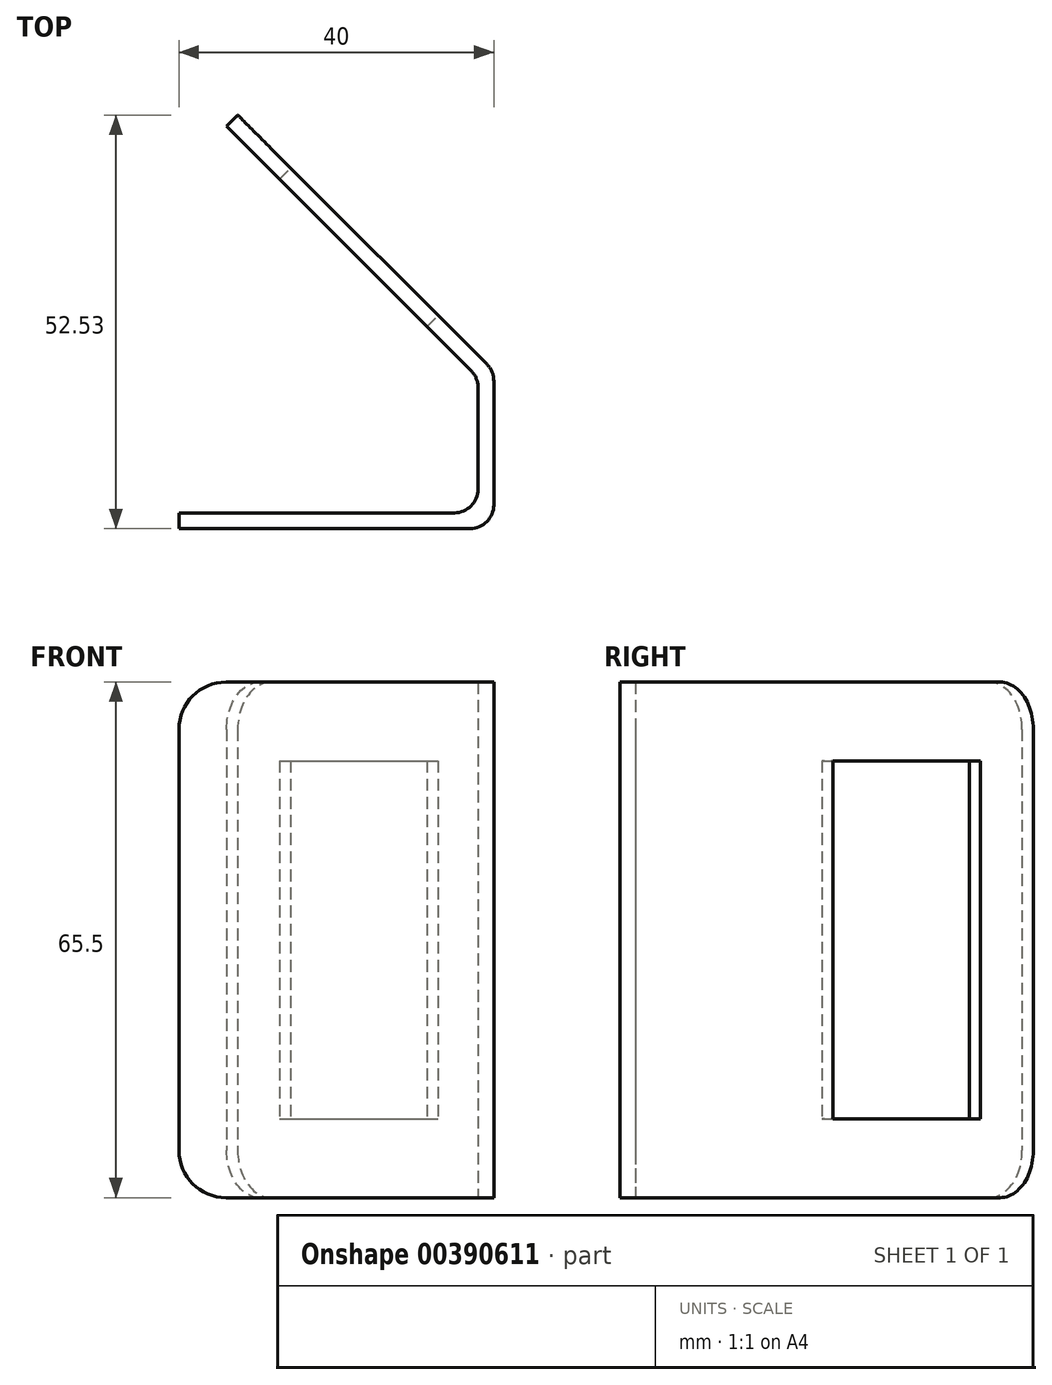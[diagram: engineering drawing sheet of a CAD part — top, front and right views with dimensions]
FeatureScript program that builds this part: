
annotation { "Feature Type Name" : "Feature", "Feature Type Description" : "" }
export const myFeature = defineFeature(function(context is Context, id is Id, definition is map)
    precondition{}
    {
        {
            var Q0;
            Q0=qCreatedBy(makeId("Top.planeOp"),FACE);
            var sketch = newSketch(context, id + "F0", { "sketchPlane" : qUnion([Q0])});
            skLineSegment(sketch, "E0", {"start": v(0, 0) * mm, "end": v(40, 0) * mm});
            skLineSegment(sketch, "E1", {"start": v(40, 0) * mm, "end": v(40, 20) * mm});
            skLineSegment(sketch, "E2", {"start": v(40, 20) * mm, "end": v(7.47, 52.53) * mm});
            skLineSegment(sketch, "E3", {"start": v(49.42, 20) * mm, "end": v(-18.7, 20) * mm, "construction": true});
            skLineSegment(sketch, "E4", {"start": v(7.47, 52.53) * mm, "end": v(6.06, 51.11) * mm});
            skLineSegment(sketch, "E5", {"start": v(6.06, 51.11) * mm, "end": v(38, 19.17) * mm});
            skLineSegment(sketch, "E6", {"start": v(38, 19.17) * mm, "end": v(38, 2) * mm});
            skLineSegment(sketch, "E7", {"start": v(38, 2) * mm, "end": v(0, 2) * mm});
            skLineSegment(sketch, "E8", {"start": v(0, 2) * mm, "end": v(0, 0) * mm});
            skSolve(sketch);
        }
        {
            var Q0;
            Q0=makeQuery(id+"F0.imprint","IMPRINT",FACE,{"disambiguationData":[TD([[makeQuery(id+"F0.imprint","IMPRINT",EDGE,{"derivedFrom":sQuery(id+"F0.wireOp",EDGE,"E0")}),1.0]])]});
            extrude(context, id + "F1", {"entities" : qUnion([Q0]), "depth" : 65.5 * mm, "offsetDistance" : 25 * mm});
        }
        {
            var Q0;
            Q0=makeQuery(id+"F1.opExtrude","SWEPT_FACE",FACE,{"disambiguationData":[OSD([sQuery(id+"F0.wireOp",EDGE,"E2")])]});
            var sketch = newSketch(context, id + "F2", { "sketchPlane" : qUnion([Q0])});
            skLineSegment(sketch, "E9.bottom", {"start": v(22.36, 55.5) * mm, "end": v(-4.14, 55.5) * mm});
            skLineSegment(sketch, "E9.top", {"start": v(22.36, 10) * mm, "end": v(-4.14, 10) * mm});
            skLineSegment(sketch, "E9.left", {"start": v(22.36, 55.5) * mm, "end": v(22.36, 10) * mm});
            skLineSegment(sketch, "E9.right", {"start": v(-4.14, 55.5) * mm, "end": v(-4.14, 10) * mm});
            skSolve(sketch);
        }
        {
            var Q0;
            Q0=makeQuery(id+"F2.imprint","IMPRINT",FACE,{"disambiguationData":[TD([[makeQuery(id+"F2.imprint","IMPRINT",EDGE,{"derivedFrom":sQuery(id+"F2.wireOp",EDGE,"E9.bottom")}),1.0]])]});
            extrude(context, id + "F3", {"entities" : qUnion([Q0]), "operationType" : NewBodyOperationType.REMOVE, "oppositeDirection" : true, "depth" : 5 * mm, "offsetDistance" : 25 * mm});
        }
        {
            var Q0;
            Q0=makeQuery(id+"F1.opExtrude","CAP_EDGE",EDGE,{"disambiguationData":[OSD([sQuery(id+"F0.wireOp",EDGE,"E4")])],"isStart":false});
            var Q1;
            Q1=makeQuery(id+"F1.opExtrude","CAP_EDGE",EDGE,{"disambiguationData":[OSD([sQuery(id+"F0.wireOp",EDGE,"E4")])],"isStart":true});
            var Q2;
            Q2=makeQuery(id+"F1.opExtrude","CAP_EDGE",EDGE,{"disambiguationData":[OSD([sQuery(id+"F0.wireOp",EDGE,"E8")])],"isStart":true});
            var Q3;
            Q3=makeQuery(id+"F1.opExtrude","CAP_EDGE",EDGE,{"disambiguationData":[OSD([sQuery(id+"F0.wireOp",EDGE,"E8")])],"isStart":false});
            fillet(context, id + "F4", {"entities" : qUnion([Q0, Q1, Q2, Q3]), "radius" : 6 * mm, "tangentPropagation" : true, "allowEdgeOverflow" : false});
        }
        {
            var Q0;
            Q0=makeQuery(id+"F1.opExtrude","SWEPT_EDGE",EDGE,{"disambiguationData":[OSD([sQuery(id+"F0.wireOp",EDGE,"E1"),sQuery(id+"F0.wireOp",EDGE,"E2")])]});
            var Q1;
            Q1=makeQuery(id+"F1.opExtrude","SWEPT_EDGE",EDGE,{"disambiguationData":[OSD([sQuery(id+"F0.wireOp",EDGE,"E5"),sQuery(id+"F0.wireOp",EDGE,"E6")])]});
            var Q2;
            Q2=makeQuery(id+"F1.opExtrude","SWEPT_EDGE",EDGE,{"disambiguationData":[OSD([sQuery(id+"F0.wireOp",EDGE,"E6"),sQuery(id+"F0.wireOp",EDGE,"E7")])]});
            var Q3;
            Q3=makeQuery(id+"F1.opExtrude","SWEPT_EDGE",EDGE,{"disambiguationData":[OSD([sQuery(id+"F0.wireOp",EDGE,"E0"),sQuery(id+"F0.wireOp",EDGE,"E1")])]});
            fillet(context, id + "F5", {"entities" : qUnion([Q0, Q1, Q2, Q3]), "radius" : 3 * mm, "tangentPropagation" : true, "allowEdgeOverflow" : false});
        }
    });
